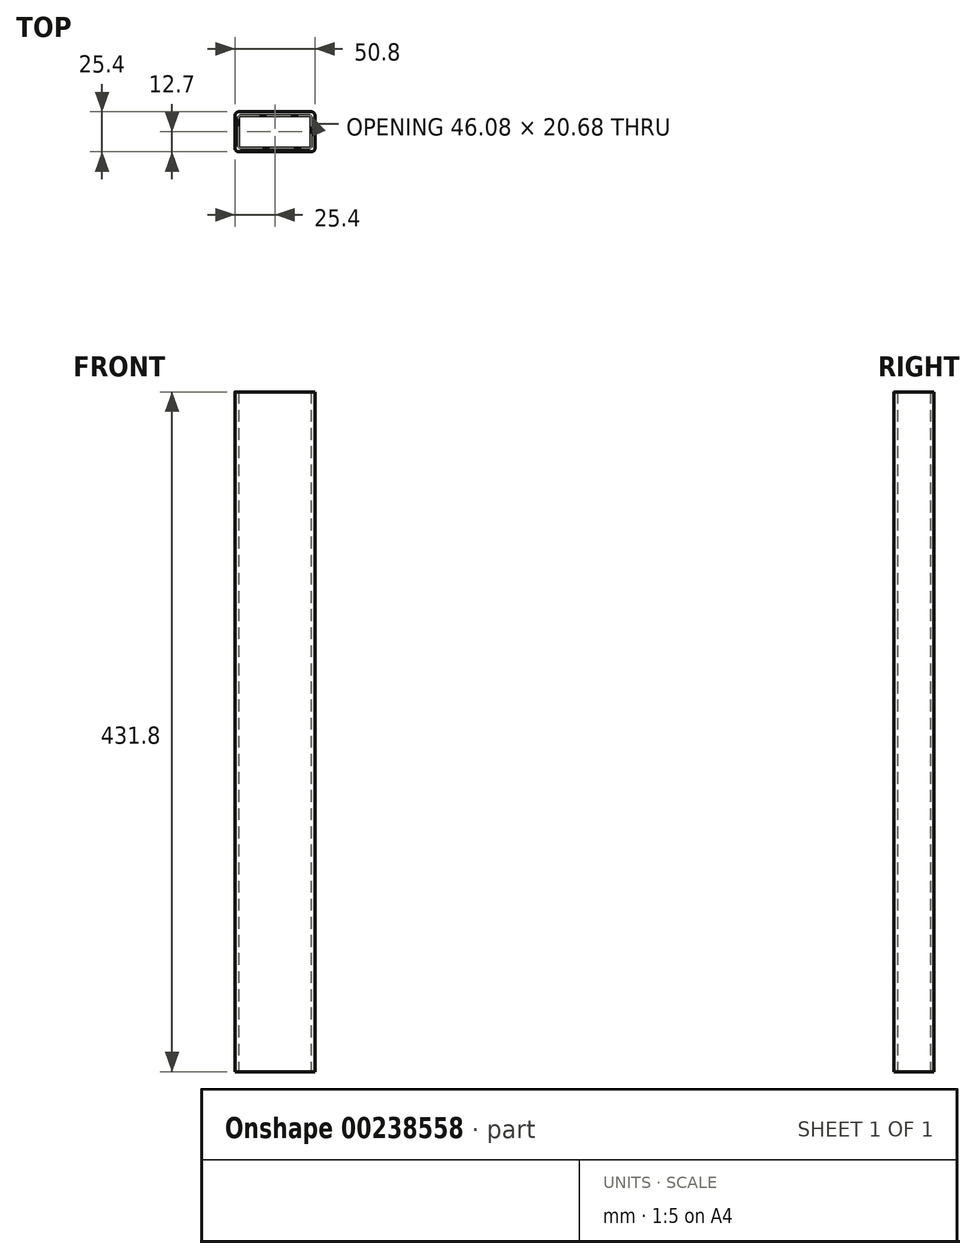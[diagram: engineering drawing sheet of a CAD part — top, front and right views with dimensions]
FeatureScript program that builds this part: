
annotation { "Feature Type Name" : "Feature", "Feature Type Description" : "" }
export const myFeature = defineFeature(function(context is Context, id is Id, definition is map)
    precondition{}
    {
        {
            var Q0;
            Q0=qCreatedBy(makeId("Top.planeOp"),FACE);
            var sketch = newSketch(context, id + "F0", { "sketchPlane" : qUnion([Q0])});
            skLineSegment(sketch, "E0", {"start": v(-25.4, 10.34) * mm, "end": v(-25.4, -10.34) * mm});
            skLineSegment(sketch, "E1", {"start": v(-23.04, -12.7) * mm, "end": v(23.04, -12.7) * mm});
            skLineSegment(sketch, "E2", {"start": v(25.4, -10.34) * mm, "end": v(25.4, 10.34) * mm});
            skLineSegment(sketch, "E3", {"start": v(23.04, 12.7) * mm, "end": v(-23.04, 12.7) * mm});
            skLineSegment(sketch, "E4", {"start": v(0, 12.7) * mm, "end": v(0, -12.7) * mm, "construction": true});
            skLineSegment(sketch, "E5", {"start": v(-25.4, 0) * mm, "end": v(25.4, 0) * mm, "construction": true});
            skPoint(sketch, "E6", {"position": v(0, 0) * mm});
            skPoint(sketch, "E7.visualSharp", {"position": v(-25.4, 12.7) * mm});
            skArc(sketch, "E7.filletArc", {"start": v(-23.04, 12.7) * mm, "mid": v(-24.7, 12) * mm, "end": v(-25.4, 10.34) * mm});
            skPoint(sketch, "E8.visualSharp", {"position": v(25.4, 12.7) * mm});
            skArc(sketch, "E8.filletArc", {"start": v(25.4, 10.34) * mm, "mid": v(24.7, 12) * mm, "end": v(23.04, 12.7) * mm});
            skPoint(sketch, "E9.visualSharp", {"position": v(25.4, -12.7) * mm});
            skArc(sketch, "E9.filletArc", {"start": v(23.04, -12.7) * mm, "mid": v(24.7, -12) * mm, "end": v(25.4, -10.34) * mm});
            skPoint(sketch, "E10.visualSharp", {"position": v(-25.4, -12.7) * mm});
            skArc(sketch, "E10.filletArc", {"start": v(-25.4, -10.34) * mm, "mid": v(-24.7, -12) * mm, "end": v(-23.04, -12.7) * mm});
            skLineSegment(sketch, "E11.0", {"start": v(21.51, 10.34) * mm, "end": v(-21.51, 10.34) * mm});
            skLineSegment(sketch, "E12.0", {"start": v(23.04, -8.81) * mm, "end": v(23.04, 8.81) * mm});
            skLineSegment(sketch, "E13.0", {"start": v(-21.51, -10.34) * mm, "end": v(21.51, -10.34) * mm});
            skLineSegment(sketch, "E14.0", {"start": v(-23.04, 8.81) * mm, "end": v(-23.04, -8.81) * mm});
            skArc(sketch, "E15.filletArc", {"start": v(-21.51, 10.34) * mm, "mid": v(-22.6, 9.9) * mm, "end": v(-23.04, 8.81) * mm});
            skArc(sketch, "E16.filletArc", {"start": v(23.04, 8.81) * mm, "mid": v(22.6, 9.9) * mm, "end": v(21.51, 10.34) * mm});
            skArc(sketch, "E17.filletArc", {"start": v(21.51, -10.34) * mm, "mid": v(22.6, -9.9) * mm, "end": v(23.04, -8.81) * mm});
            skArc(sketch, "E18.filletArc", {"start": v(-23.04, -8.81) * mm, "mid": v(-22.6, -9.9) * mm, "end": v(-21.51, -10.34) * mm});
            skSolve(sketch);
        }
        {
            var Q0;
            Q0=makeQuery(id+"F0.imprint","IMPRINT",FACE,{"disambiguationData":[TD([[makeQuery(id+"F0.imprint","IMPRINT",EDGE,{"derivedFrom":sQuery(id+"F0.wireOp",EDGE,"E0")}),1.0]])]});
            extrude(context, id + "F1", {"entities" : qUnion([Q0]), "depth" : 431.8 * mm});
        }
    });
